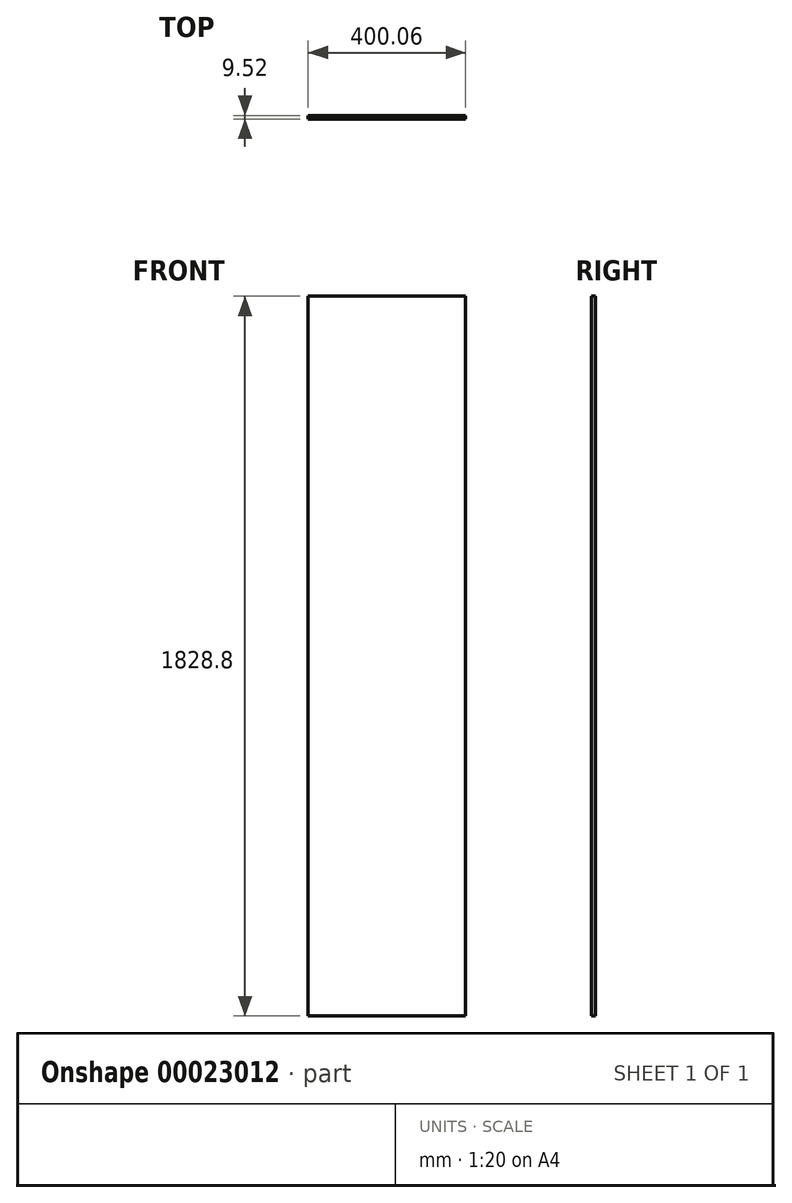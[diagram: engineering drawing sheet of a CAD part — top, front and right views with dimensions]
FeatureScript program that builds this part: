
annotation { "Feature Type Name" : "Feature", "Feature Type Description" : "" }
export const myFeature = defineFeature(function(context is Context, id is Id, definition is map)
    precondition{}
    {
        {
            var Q0;
            Q0=qCreatedBy(makeId("Top.planeOp"),FACE);
            var sketch = newSketch(context, id + "F0", { "sketchPlane" : qUnion([Q0])});
            skLineSegment(sketch, "E0.rect.bottom", {"start": v(200.03, 4.76) * mm, "end": v(-200.03, 4.76) * mm});
            skLineSegment(sketch, "E0.rect.top", {"start": v(200.02, -4.76) * mm, "end": v(-200.02, -4.76) * mm});
            skLineSegment(sketch, "E0.rect.left", {"start": v(200.03, 4.76) * mm, "end": v(200.03, -4.76) * mm});
            skLineSegment(sketch, "E0.rect.right", {"start": v(-200.03, 4.76) * mm, "end": v(-200.03, -4.76) * mm});
            skPoint(sketch, "E0.rect.middle", {"position": v(0, 0) * mm});
            skSolve(sketch);
        }
        {
            var Q0;
            Q0=makeQuery(id+"F0.imprint","IMPRINT",FACE,{"disambiguationData":[TD([[makeQuery(id+"F0.imprint","IMPRINT",EDGE,{"derivedFrom":sQuery(id+"F0.wireOp",EDGE,"E0.rect.bottom")}),1.0]])]});
            extrude(context, id + "F1", {"entities" : qUnion([Q0]), "depth" : 1828.8 * mm});
        }
    });
